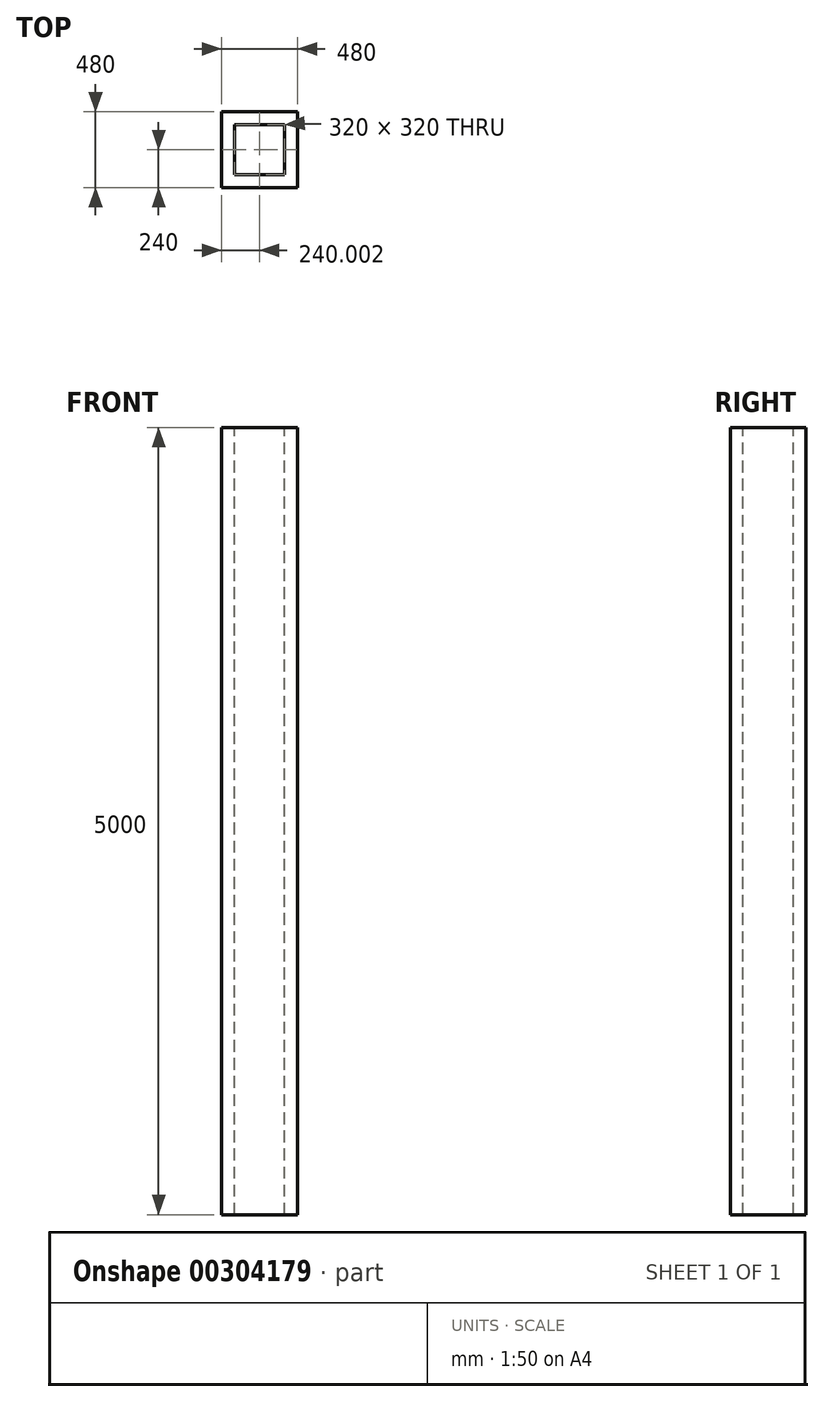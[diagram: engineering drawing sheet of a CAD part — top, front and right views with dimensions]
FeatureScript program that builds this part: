
annotation { "Feature Type Name" : "Feature", "Feature Type Description" : "" }
export const myFeature = defineFeature(function(context is Context, id is Id, definition is map)
    precondition{}
    {
        {
            var Q0;
            Q0=qCreatedBy(makeId("Top.planeOp"),FACE);
            var sketch = newSketch(context, id + "F0", { "sketchPlane" : qUnion([Q0])});
            skLineSegment(sketch, "E0.bottom", {"start": v(-40.42, 462.23) * mm, "end": v(439.58, 462.23) * mm});
            skLineSegment(sketch, "E0.top", {"start": v(-40.42, -17.77) * mm, "end": v(439.58, -17.77) * mm});
            skLineSegment(sketch, "E0.left", {"start": v(-40.42, 462.23) * mm, "end": v(-40.42, -17.77) * mm});
            skLineSegment(sketch, "E0.right", {"start": v(439.58, 462.23) * mm, "end": v(439.58, -17.77) * mm});
            skSolve(sketch);
        }
        {
            var Q0;
            Q0=makeQuery(id+"F0.imprint","IMPRINT",FACE,{"disambiguationData":[TD([[makeQuery(id+"F0.imprint","IMPRINT",EDGE,{"derivedFrom":sQuery(id+"F0.wireOp",EDGE,"E0.bottom")}),-1.0]])]});
            extrude(context, id + "F1", {"entities" : qUnion([Q0]), "depth" : 5000 * mm});
        }
        {
            var Q0;
            Q0=makeQuery(id+"F1.opExtrude","CAP_FACE",FACE,{"disambiguationData":[OSD([sQuery(id+"F0.wireOp",EDGE,"E0.bottom"),sQuery(id+"F0.wireOp",EDGE,"E0.top"),sQuery(id+"F0.wireOp",EDGE,"E0.left"),sQuery(id+"F0.wireOp",EDGE,"E0.right")])],"isStart":false});
            var sketch = newSketch(context, id + "F2", { "sketchPlane" : qUnion([Q0])});
            skLineSegment(sketch, "E1.bottom", {"start": v(39.58, 382.23) * mm, "end": v(359.58, 382.23) * mm});
            skLineSegment(sketch, "E1.top", {"start": v(39.58, 62.23) * mm, "end": v(359.58, 62.23) * mm});
            skLineSegment(sketch, "E1.left", {"start": v(39.58, 382.23) * mm, "end": v(39.58, 62.23) * mm});
            skLineSegment(sketch, "E1.right", {"start": v(359.58, 382.23) * mm, "end": v(359.58, 62.23) * mm});
            skSolve(sketch);
        }
        {
            var Q0;
            Q0=makeQuery(id+"F2.imprint","IMPRINT",FACE,{"disambiguationData":[TD([[makeQuery(id+"F2.imprint","IMPRINT",EDGE,{"derivedFrom":sQuery(id+"F2.wireOp",EDGE,"E1.bottom")}),-1.0]])]});
            extrude(context, id + "F3", {"entities" : qUnion([Q0]), "operationType" : NewBodyOperationType.REMOVE, "endBound" : BoundingType.THROUGH_ALL, "oppositeDirection" : true, "depth" : 25 * mm});
        }
    });
